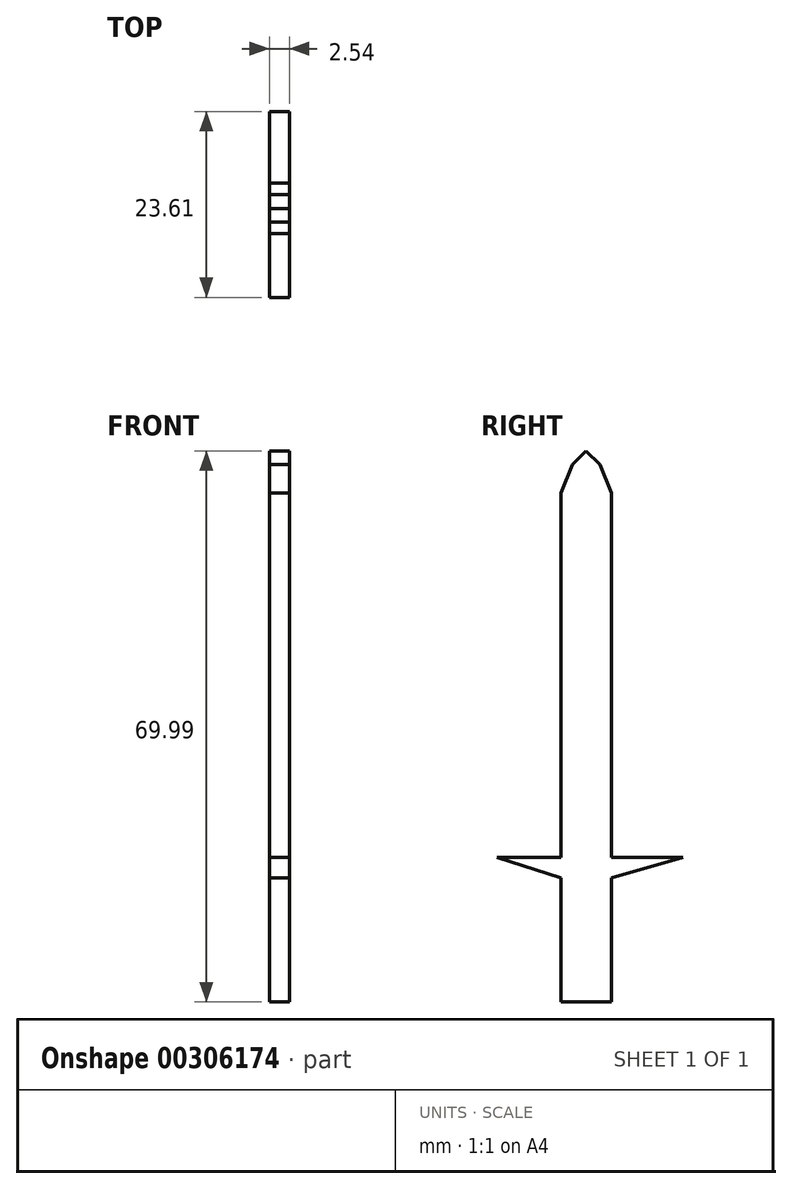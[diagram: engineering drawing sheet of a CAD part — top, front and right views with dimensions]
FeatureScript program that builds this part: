
annotation { "Feature Type Name" : "Feature", "Feature Type Description" : "" }
export const myFeature = defineFeature(function(context is Context, id is Id, definition is map)
    precondition{}
    {
        {
            var Q0;
            Q0=qCreatedBy(makeId("Right.planeOp"),FACE);
            var sketch = newSketch(context, id + "F0", { "sketchPlane" : qUnion([Q0])});
            skLineSegment(sketch, "E0", {"start": v(-49.14, -56.09) * mm, "end": v(-49.14, 0) * mm});
            skLineSegment(sketch, "E1", {"start": v(-49.14, 0) * mm, "end": v(-42.67, 0) * mm});
            skLineSegment(sketch, "E2", {"start": v(-42.67, 0) * mm, "end": v(-42.67, -56.09) * mm});
            skLineSegment(sketch, "E3", {"start": v(-49.14, -56.09) * mm, "end": v(-42.67, -56.09) * mm});
            skLineSegment(sketch, "E4", {"start": v(-42.67, -53.5) * mm, "end": v(-33.62, -53.5) * mm});
            skLineSegment(sketch, "E5", {"start": v(-33.62, -53.5) * mm, "end": v(-42.67, -56.09) * mm});
            skLineSegment(sketch, "E6", {"start": v(-49.14, -53.5) * mm, "end": v(-57.23, -53.5) * mm});
            skLineSegment(sketch, "E7", {"start": v(-57.23, -53.5) * mm, "end": v(-49.14, -56.09) * mm});
            skLineSegment(sketch, "E8", {"start": v(-49.14, -56.09) * mm, "end": v(-49.14, -71.84) * mm});
            skLineSegment(sketch, "E9", {"start": v(-49.14, -71.84) * mm, "end": v(-42.67, -71.84) * mm});
            skLineSegment(sketch, "E10", {"start": v(-42.67, -56.09) * mm, "end": v(-42.67, -71.84) * mm});
            skCircle(sketch, "E11", {"center": v(-45.9, -67.4) * mm, "radius": 3.23 * mm});
            skPoint(sketch, "E11.centerSnap0", {"position": v(-45.9, -71.84) * mm});
            skSolve(sketch);
        }
        {
            var Q0;
            Q0 = qSketchRegion(id + "F0", true);
            extrude(context, id + "F1", {"entities" : qUnion([Q0]), "depth" : 2.54 * mm});
        }
        {
            var Q0;
            Q0=makeQuery(id+"F1.opExtrude","SWEPT_EDGE",EDGE,{"disambiguationData":[OSD([sQuery(id+"F0.wireOp",EDGE,"E0"),sQuery(id+"F0.wireOp",EDGE,"E1")])]});
            var Q1;
            Q1=makeQuery(id+"F1.opExtrude","SWEPT_EDGE",EDGE,{"disambiguationData":[OSD([sQuery(id+"F0.wireOp",EDGE,"E1"),sQuery(id+"F0.wireOp",EDGE,"E2")])]});
            chamfer(context, id + "F2", {"entities" : qUnion([Q0, Q1]), "width" : 5.08 * mm, "tangentPropagation" : true});
        }
        {
            var Q0;
            Q0 = qSketchRegion(id + "F0", true);
            extrude(context, id + "F3", {"entities" : qUnion([Q0]), "operationType" : NewBodyOperationType.ADD, "depth" : 2.54 * mm});
        }
        {
            var Q0;
            Q0 = qSketchRegion(id + "F0", true);
            extrude(context, id + "F4", {"entities" : qUnion([Q0]), "operationType" : NewBodyOperationType.ADD, "depth" : 2.54 * mm});
        }
        {
            var Q0;
            Q0=makeQuery(id+"F3.opExtrude","SWEPT_EDGE",EDGE,{"disambiguationData":[OSD([sQuery(id+"F0.wireOp",EDGE,"E0"),sQuery(id+"F0.wireOp",EDGE,"E1")])]});
            var Q1;
            Q1=makeQuery(id+"F3.opExtrude","SWEPT_EDGE",EDGE,{"disambiguationData":[OSD([sQuery(id+"F0.wireOp",EDGE,"E1"),sQuery(id+"F0.wireOp",EDGE,"E2")])]});
            chamfer(context, id + "F5", {"entities" : qUnion([Q0, Q1]), "width" : 5.08 * mm, "tangentPropagation" : true});
        }
        {
            var Q0;
            {var subQ0=sQuery(id+"F0.wireOp",EDGE,"E0");Q0=makeQuery(id+"F5.opChamfer","BLEND_EDGE",EDGE,{"blendedFrom":[makeQuery(id+"F3.opExtrude","SWEPT_EDGE",EDGE,{"disambiguationData":[OSD([subQ0,sQuery(id+"F0.wireOp",EDGE,"E1")])]}),makeQuery(id+"F3.boolean.opBoolean","MERGE",FACE,{"derivedFrom":[makeQuery(id+"F1.opExtrude","SWEPT_FACE",FACE,{"disambiguationData":[OSD([subQ0])]}),makeQuery(id+"F3.opExtrude","SWEPT_FACE",FACE,{"disambiguationData":[OSD([subQ0])]})]})],"blendedInto":[makeQuery(id+"F3.boolean.opBoolean","MERGE",FACE,{"derivedFrom":[makeQuery(id+"F1.opExtrude","SWEPT_FACE",FACE,{"disambiguationData":[OSD([subQ0])]}),makeQuery(id+"F3.opExtrude","SWEPT_FACE",FACE,{"disambiguationData":[OSD([subQ0])]})]})]});}
            var Q1;
            {var subQ0=sQuery(id+"F0.wireOp",EDGE,"E2");Q1=makeQuery(id+"F5.opChamfer","BLEND_EDGE",EDGE,{"blendedFrom":[makeQuery(id+"F3.opExtrude","SWEPT_EDGE",EDGE,{"disambiguationData":[OSD([sQuery(id+"F0.wireOp",EDGE,"E1"),subQ0])]}),makeQuery(id+"F3.boolean.opBoolean","MERGE",FACE,{"derivedFrom":[makeQuery(id+"F1.opExtrude","SWEPT_FACE",FACE,{"disambiguationData":[OSD([subQ0])]}),makeQuery(id+"F3.opExtrude","SWEPT_FACE",FACE,{"disambiguationData":[OSD([subQ0])]})]})],"blendedInto":[makeQuery(id+"F3.boolean.opBoolean","MERGE",FACE,{"derivedFrom":[makeQuery(id+"F1.opExtrude","SWEPT_FACE",FACE,{"disambiguationData":[OSD([subQ0])]}),makeQuery(id+"F3.opExtrude","SWEPT_FACE",FACE,{"disambiguationData":[OSD([subQ0])]})]})]});}
            chamfer(context, id + "F6", {"entities" : qUnion([Q0, Q1]), "width" : 5.08 * mm, "tangentPropagation" : true});
        }
    });
